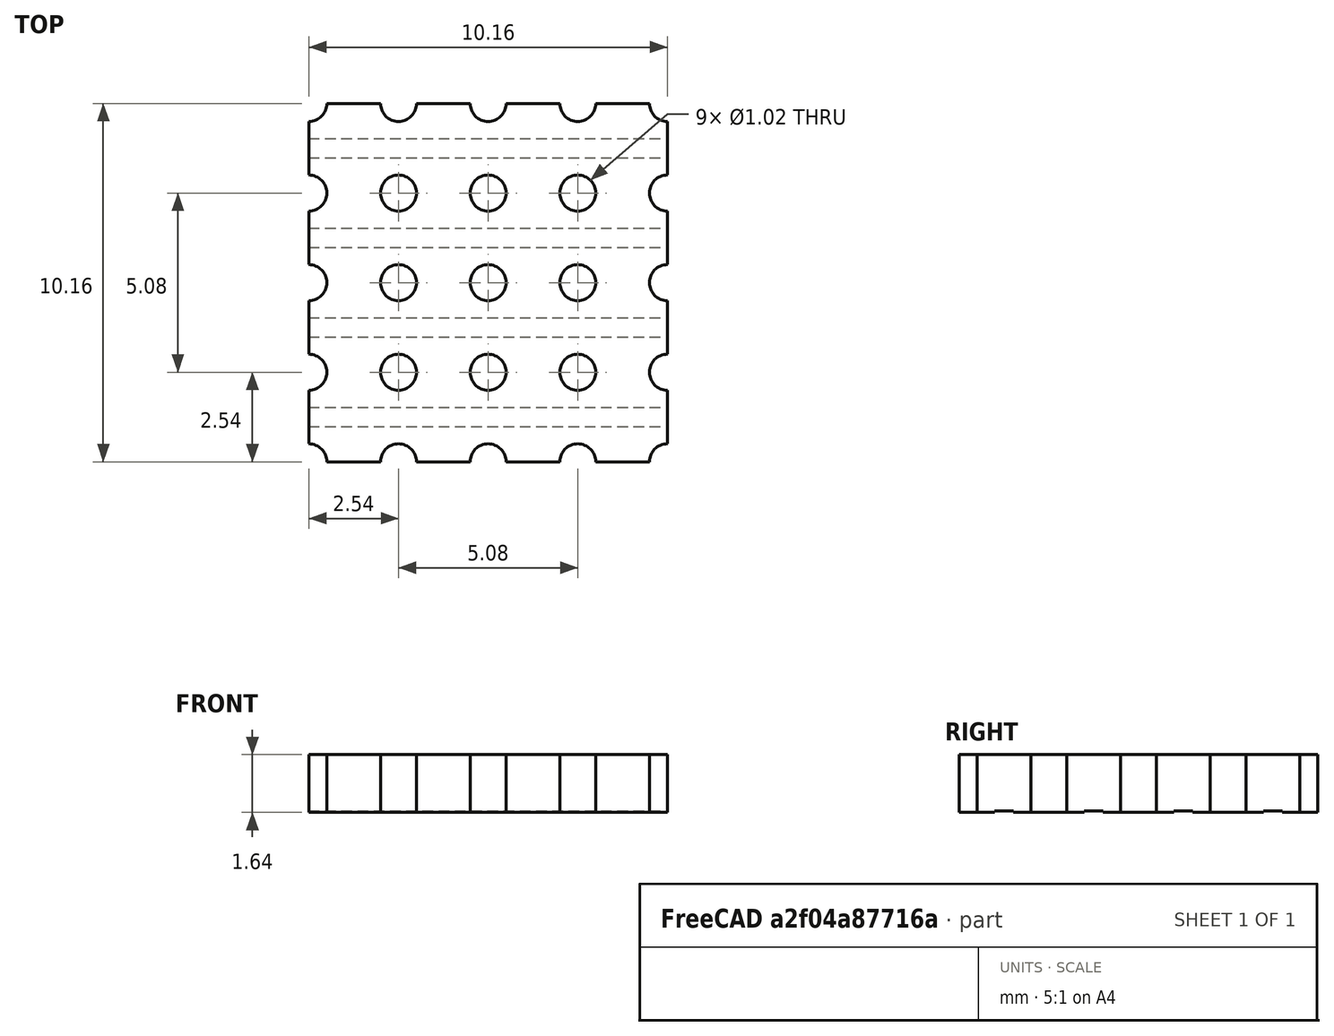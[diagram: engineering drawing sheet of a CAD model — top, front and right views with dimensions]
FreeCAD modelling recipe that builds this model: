
FCSTD DOCUMENT  (FreeCAD 0.19R16945 (Git))
Label: Vero Board Generator Part WB
License: All rights reserved
LicenseURL: http://en.wikipedia.org/wiki/All_rights_reserved
objects: Part::Box×3, Part::FeaturePython×3, Part::MultiFuse×2, Spreadsheet::Sheet×1, Part::Cylinder×1, Part::Cut×1
note: 10 computed .brp shape members not serialized (recipe doc carries the construction recipe); baked Part::Feature solids carry a one-line shape summary decoded from their .brp

FEATURE [Spreadsheet::Sheet] Spreadsheet  label="Data"
  cells = A2=diameter; B2(diameter)==1.02mm; A3=pitch_h; B3(pitch_h)==2.54mm; A4=pitch_v; B4(pitch_v)==2.54mm; A5=holes_h; B5(holes_h)=3; A6=holes_v; B6(holes_v)=3; A7=board_t; B7(board_t)==1.6mm; A8=cu_t; B8(cu_t)==35um; A9=cu_w; B9(cu_w)==2mm
FEATURE [Part::Box] Box  label="CubeBoard"
  AttacherType = Attacher::AttachEngine3D
  Height = 1.6
  Length = 10.16
  Width = 10.16
  expr: Height = Data.board_t
  expr: Width = (Data.holes_v + 1) * Data.pitch_v
  expr: Length = (Data.holes_h + 1) * Data.pitch_h
FEATURE [Part::Cylinder] Cylinder
  Angle = 360
  AttacherType = Attacher::AttachEngine3D
  Height = 3.2
  Placement = pos=(0,0,-0.8) rot=(0,0,1;0rad)
  Radius = 0.51
  expr: Placement.Base.z = -Data.board_t / 2
  expr: Height = Data.board_t * 2
  expr: Radius = Data.diameter / 2
FEATURE [Part::Box] Box001  label="CubeCopperStripFull"
  AttacherType = Attacher::AttachEngine3D
  Height = 0.035
  Length = 10.16
  Placement = pos=(0,1.54,-0.035) rot=(0,0,1;0rad)
  Width = 2
  expr: Placement.Base.y = -Data.cu_w / 2 + Data.pitch_v
  expr: Placement.Base.z = -Data.cu_t
  expr: Height = Data.cu_t
  expr: Width = Data.cu_w
  expr: Length = (Data.holes_h + 1) * Data.pitch_h
FEATURE [Part::FeaturePython] Array001  label="ArrayCylinders"  # Draft array (typed FeaturePython)
  Angle = 360
  ArrayType = 0
  Axis = (0,0,1)
  Base = -> Cylinder
  Center = (0,0,0)
  Fuse = false
  IntervalAxis = (0,0,0)
  IntervalX = (2.54,0,0)
  IntervalY = (0,2.54,0)
  IntervalZ = (0,0,1)
  NumberPolar = 1
  NumberX = 5
  NumberY = 5
  NumberZ = 1
  expr: NumberY = Data.holes_v + 2
  expr: NumberX = Data.holes_h + 2
  expr: IntervalY.y = Data.pitch_v
  expr: IntervalX.x = Data.pitch_h
FEATURE [Part::Box] Box002  label="CubeCopperStripHalf"
  AttacherType = Attacher::AttachEngine3D
  Height = 0.035
  Length = 10.16
  Placement = pos=(0,0,-0.035) rot=(0,0,1;0rad)
  Width = 1
  expr: Placement.Base.z = -Data.cu_t
  expr: Height = Data.cu_t
  expr: Width = Data.cu_w / 2
  expr: Length = (Data.holes_h + 1) * Data.pitch_h
FEATURE [Part::FeaturePython] Array  # Draft array (typed FeaturePython)
  Angle = 360
  ArrayType = 0
  Axis = (0,0,1)
  Base = -> Box001
  Center = (0,0,0)
  Fuse = false
  IntervalAxis = (0,0,0)
  IntervalX = (1,0,0)
  IntervalY = (0,2.54,0)
  IntervalZ = (0,0,1)
  NumberPolar = 1
  NumberX = 1
  NumberY = 3
  NumberZ = 1
  expr: NumberY = Data.holes_v
  expr: IntervalY.y = Data.pitch_v
FEATURE [Part::FeaturePython] Array002  # Draft array (typed FeaturePython)
  Angle = 360
  ArrayType = 0
  Axis = (0,0,1)
  Base = -> Box002
  Center = (0,0,0)
  Fuse = false
  IntervalAxis = (0,0,0)
  IntervalX = (1,0,0)
  IntervalY = (0,9.16,0)
  IntervalZ = (0,0,1)
  NumberPolar = 1
  NumberX = 1
  NumberY = 2
  NumberZ = 1
  expr: IntervalY.y = (Data.holes_v + 1) * Data.pitch_v - Data.cu_w / 2
FEATURE [Part::MultiFuse] Fusion
  Shapes = -> [Array,Array002]
FEATURE [Part::MultiFuse] Fusion001
  Shapes = -> [Box,Fusion]
FEATURE [Part::Cut] Cut
  Base = -> Fusion001
  Tool = -> Array001
